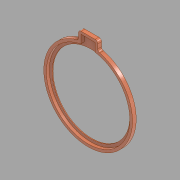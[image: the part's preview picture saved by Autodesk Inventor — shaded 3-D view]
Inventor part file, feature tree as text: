
AUTODESK INVENTOR PART (.ipt)
format: ipt  version: 2020 (Build 240168000, 168)  size: 621,568 bytes
history: native  units: mm
features: extrude x7, sketch x3, other x2, fillet x1, thicken_offset x1, chamfer x1, pattern_circular x1
ambient origin geometry x8: Origin, YZ Plane, XZ Plane, XY Plane, X Axis, Y Axis, Z Axis, Center Point
bodies: Body1 (feature_tree), Body2 (feature_tree)
feature tree (16):
  other  "CNC"
  sketch  "Sketch1"  dims[d0=16.666667mm d7=10.0mm d9=10.0mm d10=0.0mm]
  extrude  "Extrusion1"  Depth=10.0mm TaperAngle=0.0deg
  extrude  "Extrusion2"  Depth=21.2mm
  sketch  "Sketch4"  dims[d11=10.8mm d12=21.2mm]
  extrude  "Extrusion9"  Depth=2.8mm
  extrude  "Extrusion10"  Depth=10.0mm
  extrude  "Extrusion11"  Depth=3.0mm
  fillet  "Fillet2"  Radius=0.7mm
  thicken_offset  "Thicken1"
  sketch  "Sketch11"  dims[d13=0.0mm d14=2.8mm d32=10.0mm d33=5.0mm d44=29.0mm d45=0.7mm d46=52.0mm d53=10.0mm d54=0.0mm d55=11.2mm d56=0.0mm d57=10.0mm d58=0.0mm d63=0.7mm d70=2.8mm d71=10.0mm d91=0.2mm d95=1.75mm d129=0.7mm d144=0.7mm d145=0.0mm d146=7.0mm d147=7.0mm d149=8.0mm d150=3.0mm d151=0.42237mm d152=0.2mm d153=0.0mm d154=5.0mm d155=0.0mm d156=3.0mm d157=2.0mm d158=45.0deg d159=600.0mm d160=360.0deg d77=0.5mm d78=0.872665mm d79=0.5mm d80=0.872665mm]
  extrude  "Extrusion19"  Depth=3.0mm
  extrude  "Extrusion20"  Depth=10.0mm TaperAngle=0.0deg
  chamfer  "Chamfer4"  Distance=11.2mm
  pattern_circular  "Circular Pattern3"  [2 undecoded]
  other  "3D print inset"
note: 2 required parameter values undecoded (feature->parameter linkage not recoverable at this tier; creation-order binding heuristic only, values carry confidence <= 0.55)
